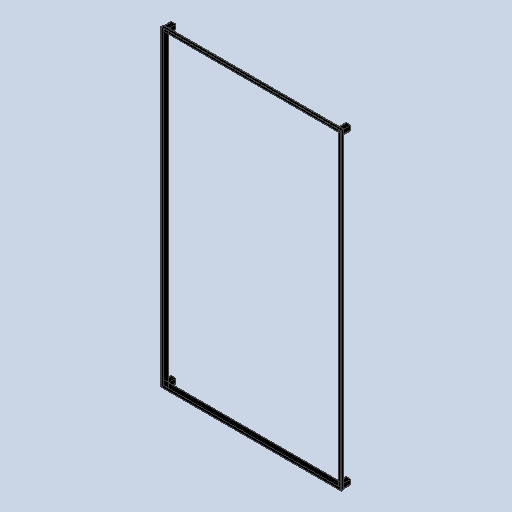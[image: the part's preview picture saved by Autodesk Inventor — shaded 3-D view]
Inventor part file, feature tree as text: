
AUTODESK INVENTOR PART (.ipt)
format: ipt  version: 2025 (Build 290162000, 162)  size: 164,352 bytes
history: native  units: mm
features: extrude x2, shell x2, projected_geometry x1, sketch x1
ambient origin geometry x8: Origin, YZ Plane, XZ Plane, XY Plane, X Axis, Y Axis, Z Axis, Center Point
bodies: Solid1 (feature_tree), Solid2 (feature_tree)
feature tree (6):
  extrude  "Extrusion1"  Depth=2600.0mm
  shell  "Shell1"  Thickness=40.0mm
  extrude  "Extrusion2"  Depth=20.0mm TaperAngle=0.0deg
  shell  "Shell2"  Thickness=3.0mm
  projected_geometry  "Projected Loop1"
  sketch  "Sketch Rectangular Pattern1"  dims[d0=1500.0mm d1=2600.0mm d2=40.0mm d3=20.0mm d4=0.0mm d5=3.0mm d6=20.0mm d8=1460.0mm d9=20.0mm d11=2560.0mm d14=60.0mm d15=0.0mm d16=3.0mm]
